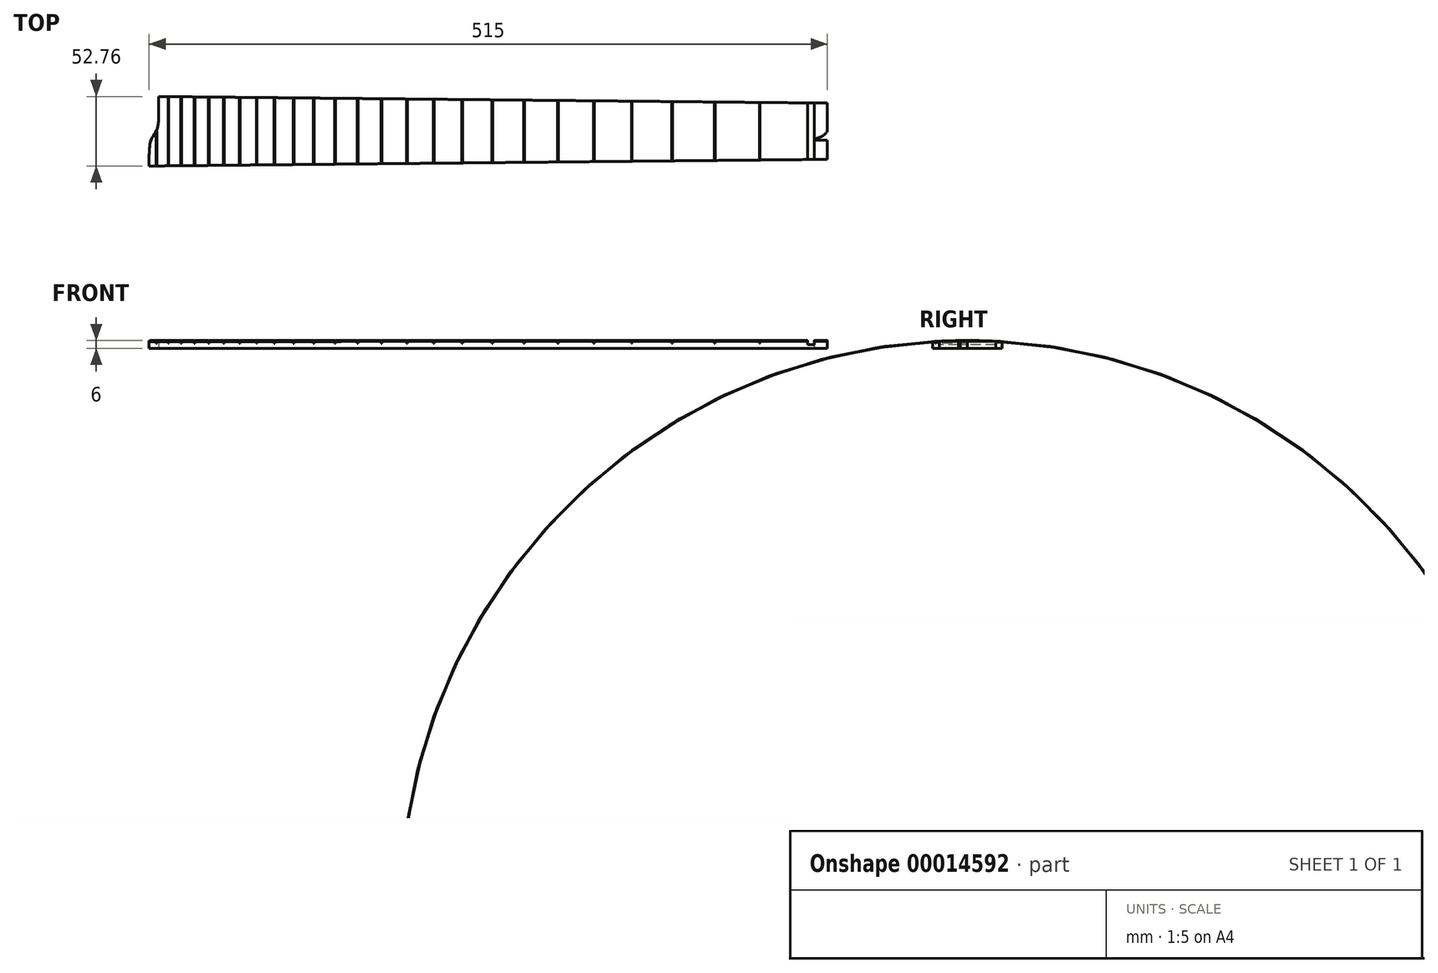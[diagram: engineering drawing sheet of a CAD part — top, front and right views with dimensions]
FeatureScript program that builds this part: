
annotation { "Feature Type Name" : "Feature", "Feature Type Description" : "" }
export const myFeature = defineFeature(function(context is Context, id is Id, definition is map)
    precondition{}
    {
        {
            var Q0;
            Q0=qCreatedBy(makeId("Top.planeOp"),FACE);
            var sketch = newSketch(context, id + "F0", { "sketchPlane" : qUnion([Q0])});
            skLineSegment(sketch, "E0", {"start": v(0, 159.31) * mm, "end": v(0, -181.23) * mm, "construction": true});
            skLineSegment(sketch, "E1", {"start": v(500, 123.18) * mm, "end": v(500, -150.63) * mm, "construction": true});
            skLineSegment(sketch, "E2", {"start": v(0, 0) * mm, "end": v(0, 26.42) * mm});
            skLineSegment(sketch, "E3", {"start": v(0, 26.42) * mm, "end": v(500, 21.5) * mm});
            skLineSegment(sketch, "E4", {"start": v(500, 21.5) * mm, "end": v(500, 0) * mm});
            skLineSegment(sketch, "E5", {"start": v(-118.15, 0) * mm, "end": v(589.57, 0) * mm, "construction": true});
            skLineSegment(sketch, "E6.0.MirrorCS", {"start": v(0, 0) * mm, "end": v(0, -26.42) * mm});
            skLineSegment(sketch, "E7.0.MirrorCS", {"start": v(0, -26.42) * mm, "end": v(500, -21.5) * mm});
            skLineSegment(sketch, "E8.0.MirrorCS", {"start": v(500, -21.5) * mm, "end": v(500, 0) * mm});
            skSolve(sketch);
        }
        {
            var Q0;
            Q0=makeQuery(id+"F0.imprint","IMPRINT",FACE,{"disambiguationData":[TD([[makeQuery(id+"F0.imprint","IMPRINT",EDGE,{"derivedFrom":sQuery(id+"F0.wireOp",EDGE,"E2")}),-1.0]])]});
            extrude(context, id + "F1", {"entities" : qUnion([Q0]), "depth" : 6 * mm});
        }
        {
            var Q0;
            Q0=qCreatedBy(makeId("Right.planeOp"),FACE);
            var sketch = newSketch(context, id + "F2", { "sketchPlane" : qUnion([Q0])});
            skCircle(sketch, "E9", {"center": v(0, -424) * mm, "radius": 430 * mm});
            skSolve(sketch);
        }
        {
            var Q0;
            Q0=makeQuery(id+"F2.imprint","IMPRINT",FACE,{"disambiguationData":[TD([[makeQuery(id+"F2.imprint","IMPRINT",EDGE,{"derivedFrom":sQuery(id+"F2.wireOp",EDGE,"E9")}),1.0]])]});
            var Q1;
            Q1=makeQuery(id+"F1.opExtrude","SWEPT_BODY",BODY,{"disambiguationData":[OSD([sQuery(id+"F0.wireOp",EDGE,"E2"),sQuery(id+"F0.wireOp",EDGE,"E3"),sQuery(id+"F0.wireOp",EDGE,"E4"),sQuery(id+"F0.wireOp",EDGE,"E6.0.MirrorCS"),sQuery(id+"F0.wireOp",EDGE,"E7.0.MirrorCS"),sQuery(id+"F0.wireOp",EDGE,"E8.0.MirrorCS")])]});
            extrude(context, id + "F3", {"entities" : qUnion([Q0]), "endBoundEntity" : qUnion([Q1]), "depth" : 500 * mm});
        }
        {
            var Q0;
            Q0=makeQuery(id+"F3.opExtrude","SWEPT_BODY",BODY,{"disambiguationData":[OSD([sQuery(id+"F2.wireOp",EDGE,"E9")])]});
            var Q1;
            Q1=makeQuery(id+"F1.opExtrude","SWEPT_BODY",BODY,{"disambiguationData":[OSD([sQuery(id+"F0.wireOp",EDGE,"E2"),sQuery(id+"F0.wireOp",EDGE,"E3"),sQuery(id+"F0.wireOp",EDGE,"E4"),sQuery(id+"F0.wireOp",EDGE,"E6.0.MirrorCS"),sQuery(id+"F0.wireOp",EDGE,"E7.0.MirrorCS"),sQuery(id+"F0.wireOp",EDGE,"E8.0.MirrorCS")])]});
            booleanBodies(context, id + "F4", {"operationType" : BooleanOperationType.INTERSECTION, "tools" : qUnion([Q0, Q1])});
        }
        {
            var Q0;
            Q0=qCreatedBy(makeId("Top.planeOp"),FACE);
            cPlane(context, id + "F5", {"entities" : qUnion([Q0]), "cplaneType" : CPlaneType.OFFSET, "offset" : 4 * mm, "width" : 150 * mm, "height" : 150 * mm});
        }
        {
            var Q0;
            Q0=qCreatedBy(id+"F5.planeOp",FACE);
            var sketch = newSketch(context, id + "F6", { "sketchPlane" : qUnion([Q0])});
            skLineSegment(sketch, "E10.bottom", {"start": v(463.4, 30) * mm, "end": v(463.98, 30) * mm});
            skLineSegment(sketch, "E10.top", {"start": v(463.4, -30) * mm, "end": v(463.98, -30) * mm});
            skLineSegment(sketch, "E10.left", {"start": v(463.4, 30) * mm, "end": v(463.4, -30) * mm});
            skLineSegment(sketch, "E10.right", {"start": v(463.98, 30) * mm, "end": v(463.98, -30) * mm});
            skLineSegment(sketch, "E11", {"start": v(-58.5, 0) * mm, "end": v(562.56, 0) * mm, "construction": true});
            skLineSegment(sketch, "E12.right", {"start": v(429.7, 30) * mm, "end": v(429.7, -30) * mm});
            skLineSegment(sketch, "E12.left", {"start": v(429.12, 30) * mm, "end": v(429.12, -30) * mm});
            skLineSegment(sketch, "E12.top", {"start": v(429.12, -30) * mm, "end": v(429.7, -30) * mm});
            skLineSegment(sketch, "E12.bottom", {"start": v(429.12, 30) * mm, "end": v(429.7, 30) * mm});
            skLineSegment(sketch, "E13.right", {"start": v(397.35, 30) * mm, "end": v(397.35, -30) * mm});
            skLineSegment(sketch, "E13.left", {"start": v(396.77, 30) * mm, "end": v(396.77, -30) * mm});
            skLineSegment(sketch, "E13.top", {"start": v(396.77, -30) * mm, "end": v(397.35, -30) * mm});
            skLineSegment(sketch, "E13.bottom", {"start": v(396.77, 30) * mm, "end": v(397.35, 30) * mm});
            skLineSegment(sketch, "E14.right", {"start": v(366.8, 30) * mm, "end": v(366.8, -30) * mm});
            skLineSegment(sketch, "E14.left", {"start": v(366.23, 30) * mm, "end": v(366.23, -30) * mm});
            skLineSegment(sketch, "E14.top", {"start": v(366.23, -30) * mm, "end": v(366.8, -30) * mm});
            skLineSegment(sketch, "E14.bottom", {"start": v(366.23, 30) * mm, "end": v(366.8, 30) * mm});
            skLineSegment(sketch, "E15.right", {"start": v(337.99, 30) * mm, "end": v(337.99, -30) * mm});
            skLineSegment(sketch, "E15.left", {"start": v(337.4, 30) * mm, "end": v(337.4, -30) * mm});
            skLineSegment(sketch, "E15.top", {"start": v(337.4, -30) * mm, "end": v(337.99, -30) * mm});
            skLineSegment(sketch, "E15.bottom", {"start": v(337.4, 30) * mm, "end": v(337.99, 30) * mm});
            skLineSegment(sketch, "E16.right", {"start": v(310.79, 30) * mm, "end": v(310.79, -30) * mm});
            skLineSegment(sketch, "E16.left", {"start": v(310.2, 30) * mm, "end": v(310.2, -30) * mm});
            skLineSegment(sketch, "E16.top", {"start": v(310.2, -30) * mm, "end": v(310.79, -30) * mm});
            skLineSegment(sketch, "E16.bottom", {"start": v(310.2, 30) * mm, "end": v(310.79, 30) * mm});
            skLineSegment(sketch, "E17.right", {"start": v(285.1, 30) * mm, "end": v(285.1, -30) * mm});
            skLineSegment(sketch, "E17.left", {"start": v(284.53, 30) * mm, "end": v(284.53, -30) * mm});
            skLineSegment(sketch, "E17.bottom", {"start": v(284.53, 30) * mm, "end": v(285.1, 30) * mm});
            skLineSegment(sketch, "E17.top", {"start": v(284.53, -30) * mm, "end": v(285.1, -30) * mm});
            skLineSegment(sketch, "E18.left", {"start": v(260.29, 30) * mm, "end": v(260.29, -30) * mm});
            skLineSegment(sketch, "E18.right", {"start": v(260.87, 30) * mm, "end": v(260.87, -30) * mm});
            skLineSegment(sketch, "E18.top", {"start": v(260.29, -30) * mm, "end": v(260.87, -30) * mm});
            skLineSegment(sketch, "E18.bottom", {"start": v(260.29, 30) * mm, "end": v(260.87, 30) * mm});
            skLineSegment(sketch, "E19.left", {"start": v(237.4, 30) * mm, "end": v(237.4, -30) * mm});
            skLineSegment(sketch, "E19.right", {"start": v(237.99, 30) * mm, "end": v(237.99, -30) * mm});
            skLineSegment(sketch, "E19.top", {"start": v(237.4, -30) * mm, "end": v(237.99, -30) * mm});
            skLineSegment(sketch, "E19.bottom", {"start": v(237.4, 30) * mm, "end": v(237.99, 30) * mm});
            skLineSegment(sketch, "E20.left", {"start": v(215.82, 30) * mm, "end": v(215.82, -30) * mm});
            skLineSegment(sketch, "E20.right", {"start": v(216.4, 30) * mm, "end": v(216.4, -30) * mm});
            skLineSegment(sketch, "E20.top", {"start": v(215.82, -30) * mm, "end": v(216.4, -30) * mm});
            skLineSegment(sketch, "E20.bottom", {"start": v(215.82, 30) * mm, "end": v(216.4, 30) * mm});
            skLineSegment(sketch, "E21.left", {"start": v(195.44, 30) * mm, "end": v(195.44, -30) * mm});
            skLineSegment(sketch, "E21.right", {"start": v(196.02, 30) * mm, "end": v(196.02, -30) * mm});
            skLineSegment(sketch, "E21.top", {"start": v(195.44, -30) * mm, "end": v(196.02, -30) * mm});
            skLineSegment(sketch, "E21.bottom", {"start": v(195.44, 30) * mm, "end": v(196.02, 30) * mm});
            skLineSegment(sketch, "E22.left", {"start": v(176.2, 30) * mm, "end": v(176.2, -30) * mm});
            skLineSegment(sketch, "E22.right", {"start": v(176.78, 30) * mm, "end": v(176.78, -30) * mm});
            skLineSegment(sketch, "E22.top", {"start": v(176.2, -30) * mm, "end": v(176.78, -30) * mm});
            skLineSegment(sketch, "E22.bottom", {"start": v(176.2, 30) * mm, "end": v(176.78, 30) * mm});
            skLineSegment(sketch, "E23.left", {"start": v(158.04, 30) * mm, "end": v(158.04, -30) * mm});
            skLineSegment(sketch, "E23.right", {"start": v(158.62, 30) * mm, "end": v(158.62, -30) * mm});
            skLineSegment(sketch, "E23.top", {"start": v(158.04, -30) * mm, "end": v(158.62, -30) * mm});
            skLineSegment(sketch, "E23.bottom", {"start": v(158.04, 30) * mm, "end": v(158.62, 30) * mm});
            skLineSegment(sketch, "E24.left", {"start": v(140.9, 30) * mm, "end": v(140.9, -30) * mm});
            skLineSegment(sketch, "E24.right", {"start": v(141.48, 30) * mm, "end": v(141.48, -30) * mm});
            skLineSegment(sketch, "E24.top", {"start": v(140.9, -30) * mm, "end": v(141.48, -30) * mm});
            skLineSegment(sketch, "E24.bottom", {"start": v(140.9, 30) * mm, "end": v(141.48, 30) * mm});
            skLineSegment(sketch, "E25.left", {"start": v(124.72, 30) * mm, "end": v(124.72, -30) * mm});
            skLineSegment(sketch, "E25.right", {"start": v(125.3, 30) * mm, "end": v(125.3, -30) * mm});
            skLineSegment(sketch, "E25.top", {"start": v(124.72, -30) * mm, "end": v(125.3, -30) * mm});
            skLineSegment(sketch, "E25.bottom", {"start": v(124.72, 30) * mm, "end": v(125.3, 30) * mm});
            skLineSegment(sketch, "E26.left", {"start": v(109.45, 30) * mm, "end": v(109.45, -30) * mm});
            skLineSegment(sketch, "E26.right", {"start": v(110.03, 30) * mm, "end": v(110.03, -30) * mm});
            skLineSegment(sketch, "E26.top", {"start": v(109.45, -30) * mm, "end": v(110.03, -30) * mm});
            skLineSegment(sketch, "E26.bottom", {"start": v(109.45, 30) * mm, "end": v(110.03, 30) * mm});
            skLineSegment(sketch, "E27.left", {"start": v(95.04, 30) * mm, "end": v(95.04, -30) * mm});
            skLineSegment(sketch, "E27.right", {"start": v(95.62, 30) * mm, "end": v(95.62, -30) * mm});
            skLineSegment(sketch, "E27.top", {"start": v(95.04, -30) * mm, "end": v(95.62, -30) * mm});
            skLineSegment(sketch, "E27.bottom", {"start": v(95.04, 30) * mm, "end": v(95.62, 30) * mm});
            skLineSegment(sketch, "E28.left", {"start": v(81.44, 30) * mm, "end": v(81.44, -30) * mm});
            skLineSegment(sketch, "E28.right", {"start": v(82.02, 30) * mm, "end": v(82.02, -30) * mm});
            skLineSegment(sketch, "E28.top", {"start": v(81.44, -30) * mm, "end": v(82.02, -30) * mm});
            skLineSegment(sketch, "E28.bottom", {"start": v(81.44, 30) * mm, "end": v(82.02, 30) * mm});
            skLineSegment(sketch, "E29.left", {"start": v(68.6, 30) * mm, "end": v(68.6, -30) * mm});
            skLineSegment(sketch, "E29.right", {"start": v(69.18, 30) * mm, "end": v(69.18, -30) * mm});
            skLineSegment(sketch, "E29.top", {"start": v(68.6, -30) * mm, "end": v(69.18, -30) * mm});
            skLineSegment(sketch, "E29.bottom", {"start": v(68.6, 30) * mm, "end": v(69.18, 30) * mm});
            skLineSegment(sketch, "E30.left", {"start": v(56.48, 30) * mm, "end": v(56.48, -30) * mm});
            skLineSegment(sketch, "E30.right", {"start": v(57.06, 30) * mm, "end": v(57.06, -30) * mm});
            skLineSegment(sketch, "E30.top", {"start": v(56.48, -30) * mm, "end": v(57.06, -30) * mm});
            skLineSegment(sketch, "E30.bottom", {"start": v(56.48, 30) * mm, "end": v(57.06, 30) * mm});
            skLineSegment(sketch, "E31.left", {"start": v(45.04, 30) * mm, "end": v(45.04, -30) * mm});
            skLineSegment(sketch, "E31.right", {"start": v(45.62, 30) * mm, "end": v(45.62, -30) * mm});
            skLineSegment(sketch, "E31.top", {"start": v(45.04, -30) * mm, "end": v(45.62, -30) * mm});
            skLineSegment(sketch, "E31.bottom", {"start": v(45.04, 30) * mm, "end": v(45.62, 30) * mm});
            skLineSegment(sketch, "E32.left", {"start": v(34.24, 30) * mm, "end": v(34.24, -30) * mm});
            skLineSegment(sketch, "E32.right", {"start": v(34.82, 30) * mm, "end": v(34.82, -30) * mm});
            skLineSegment(sketch, "E32.top", {"start": v(34.24, -30) * mm, "end": v(34.82, -30) * mm});
            skLineSegment(sketch, "E32.bottom", {"start": v(34.24, 30) * mm, "end": v(34.82, 30) * mm});
            skLineSegment(sketch, "E33.left", {"start": v(24.05, 30) * mm, "end": v(24.05, -30) * mm});
            skLineSegment(sketch, "E33.right", {"start": v(24.63, 30) * mm, "end": v(24.63, -30) * mm});
            skLineSegment(sketch, "E33.top", {"start": v(24.05, -30) * mm, "end": v(24.63, -30) * mm});
            skLineSegment(sketch, "E33.bottom", {"start": v(24.05, 30) * mm, "end": v(24.63, 30) * mm});
            skLineSegment(sketch, "E34.left", {"start": v(14.43, 30) * mm, "end": v(14.43, -30) * mm});
            skLineSegment(sketch, "E34.right", {"start": v(15, 30) * mm, "end": v(15, -30) * mm});
            skLineSegment(sketch, "E34.top", {"start": v(14.43, -30) * mm, "end": v(15, -30) * mm});
            skLineSegment(sketch, "E34.bottom", {"start": v(14.43, 30) * mm, "end": v(15, 30) * mm});
            skLineSegment(sketch, "E35.left", {"start": v(5.34, 0) * mm, "end": v(5.34, -30) * mm});
            skLineSegment(sketch, "E35.right", {"start": v(5.92, 0) * mm, "end": v(5.92, -30) * mm});
            skLineSegment(sketch, "E35.top", {"start": v(5.34, -30) * mm, "end": v(5.92, -30) * mm});
            skLineSegment(sketch, "E35.bottom", {"start": v(5.34, 0) * mm, "end": v(5.92, 0) * mm});
            skSolve(sketch);
        }
        {
            var Q0;
            Q0=qSketchRegion(id+"F6",true);
            extrude(context, id + "F7", {"entities" : qUnion([Q0]), "operationType" : NewBodyOperationType.REMOVE, "depth" : 25 * mm});
        }
        {
            var Q0;
            Q0=qCreatedBy(makeId("Top.planeOp"),FACE);
            var sketch = newSketch(context, id + "F8", { "sketchPlane" : qUnion([Q0])});
            skPoint(sketch, "E36.0", {"position": v(0, -26.42) * mm});
            skLineSegment(sketch, "E37", {"start": v(0, -26.42) * mm, "end": v(-6.45, 29.83) * mm});
            skLineSegment(sketch, "E38", {"start": v(-6.45, 29.83) * mm, "end": v(7.22, 26.34) * mm});
            skLineSegment(sketch, "E39", {"start": v(7.22, 26.34) * mm, "end": v(-6.45, 29.83) * mm});
            skLineSegment(sketch, "E40.0", {"start": v(0, 26.42) * mm, "end": v(14.43, 26.27) * mm});
            skLineSegment(sketch, "E41", {"start": v(7.22, 26.34) * mm, "end": v(7.22, 10.5) * mm});
            skFitSpline(sketch, "E42", {"points": [v(0, -26.42) * mm, v(3.02, -3.85) * mm, v(5.28, 0) * mm, v(7.22, 10.5) * mm], "startDerivative": vector(0, 124.7) * mm, "endDerivative": vector(0, 57.98) * mm});
            skSolve(sketch);
        }
        {
            var Q0;
            Q0=qSketchRegion(id+"F8",true);
            extrude(context, id + "F9", {"entities" : qUnion([Q0]), "operationType" : NewBodyOperationType.REMOVE, "depth" : 25 * mm});
        }
        {
            var Q0;
            Q0=makeQuery(id+"F3.opExtrude","CAP_FACE",FACE,{"disambiguationData":[OSD([sQuery(id+"F2.wireOp",EDGE,"E9")])],"isStart":false});
            extrude(context, id + "F10", {"entities" : qUnion([Q0]), "operationType" : NewBodyOperationType.ADD, "depth" : 15 * mm});
        }
        {
            var Q0;
            Q0=qCreatedBy(makeId("Top.planeOp"),FACE);
            cPlane(context, id + "F11", {"entities" : qUnion([Q0]), "cplaneType" : CPlaneType.OFFSET, "offset" : 3 * mm, "width" : 150 * mm, "height" : 150 * mm});
        }
        {
            var Q0;
            Q0=qCreatedBy(id+"F11.planeOp",FACE);
            var sketch = newSketch(context, id + "F12", { "sketchPlane" : qUnion([Q0])});
            skPoint(sketch, "E43.0", {"position": v(500, 21.5) * mm});
            skPoint(sketch, "E43.1", {"position": v(500, -21.5) * mm});
            skLineSegment(sketch, "E44.bottom", {"start": v(500, 21.5) * mm, "end": v(505, 21.5) * mm});
            skLineSegment(sketch, "E44.top", {"start": v(500, -21.5) * mm, "end": v(505, -21.5) * mm});
            skLineSegment(sketch, "E44.left", {"start": v(500, 21.5) * mm, "end": v(500, -21.5) * mm});
            skLineSegment(sketch, "E44.right", {"start": v(505, 21.5) * mm, "end": v(505, -21.5) * mm});
            skSolve(sketch);
        }
        {
            var Q0;
            Q0=qSketchRegion(id+"F12",true);
            extrude(context, id + "F13", {"entities" : qUnion([Q0]), "operationType" : NewBodyOperationType.REMOVE, "depth" : 25 * mm});
        }
        {
            var Q0;
            Q0=makeQuery(id+"F10.opExtrude","SWEPT_FACE",FACE,{"disambiguationData":[OSD([sQuery(id+"F0.wireOp",EDGE,"E7.0.MirrorCS"),sQuery(id+"F0.wireOp",EDGE,"E8.0.MirrorCS")])]});
            var sketch = newSketch(context, id + "F14", { "sketchPlane" : qUnion([Q0])});
            skArc(sketch, "E45", {"start": v(515, 0) * mm, "mid": v(510.7, 4) * mm, "end": v(505, 5.46) * mm});
            skLineSegment(sketch, "E46", {"start": v(515, 0) * mm, "end": v(515.27, -0.4) * mm});
            skLineSegment(sketch, "E47", {"start": v(515.27, -0.4) * mm, "end": v(515.27, 6.83) * mm});
            skLineSegment(sketch, "E48", {"start": v(515.27, 6.83) * mm, "end": v(505, 6.83) * mm});
            skLineSegment(sketch, "E49", {"start": v(505, 6.83) * mm, "end": v(505, 5.46) * mm});
            skSolve(sketch);
        }
        {
            var Q0;
            Q0=qSketchRegion(id+"F14",true);
            extrude(context, id + "F15", {"entities" : qUnion([Q0]), "operationType" : NewBodyOperationType.REMOVE, "endBound" : BoundingType.THROUGH_ALL, "oppositeDirection" : true, "depth" : 25 * mm});
        }
        {
            var Q0;
            Q0=makeQuery(id+"F13.boolean.opBoolean","COPY",FACE,{"derivedFrom":makeQuery(id+"F13.opExtrude","SWEPT_FACE",FACE,{"disambiguationData":[OSD([sQuery(id+"F12.wireOp",EDGE,"E44.right")])]})});
            var sketch = newSketch(context, id + "F16", { "sketchPlane" : qUnion([Q0])});
            skPoint(sketch, "E50.0", {"position": v(21.5, 5.46) * mm});
            skPoint(sketch, "E50.1", {"position": v(-21.5, 5.46) * mm});
            skLineSegment(sketch, "E51.bottom", {"start": v(-24.53, 5.46) * mm, "end": v(24, 5.46) * mm});
            skLineSegment(sketch, "E51.top", {"start": v(-24.53, 12.39) * mm, "end": v(24, 12.39) * mm});
            skLineSegment(sketch, "E51.left", {"start": v(-24.53, 5.46) * mm, "end": v(-24.53, 12.39) * mm});
            skLineSegment(sketch, "E51.right", {"start": v(24, 5.46) * mm, "end": v(24, 12.39) * mm});
            skSolve(sketch);
        }
        {
            var Q0;
            Q0=makeQuery(id+"F16.imprint","IMPRINT",FACE,{"disambiguationData":[TD([[makeQuery(id+"F16.imprint","IMPRINT",EDGE,{"derivedFrom":sQuery(id+"F16.wireOp",EDGE,"E51.top")}),-1.0]])]});
            extrude(context, id + "F17", {"entities" : qUnion([Q0]), "operationType" : NewBodyOperationType.REMOVE, "endBound" : BoundingType.THROUGH_ALL, "oppositeDirection" : true, "depth" : 48.46 * mm});
        }
    });
